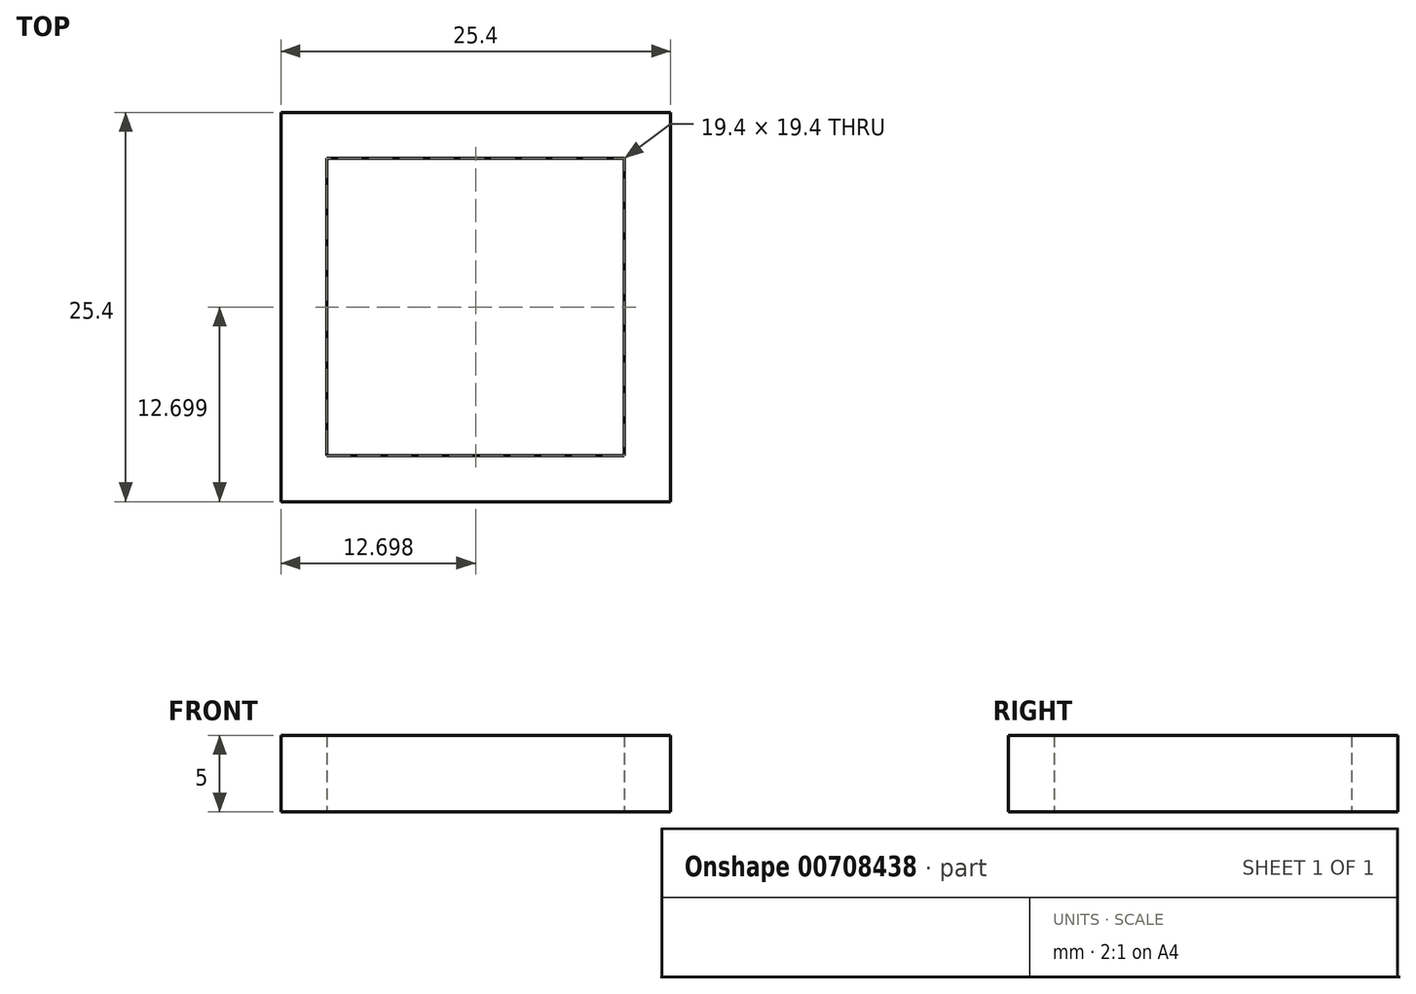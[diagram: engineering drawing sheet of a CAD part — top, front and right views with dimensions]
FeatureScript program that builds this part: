
annotation { "Feature Type Name" : "Feature", "Feature Type Description" : "" }
export const myFeature = defineFeature(function(context is Context, id is Id, definition is map)
    precondition{}
    {
        {
            var Q0;
            Q0=qCreatedBy(makeId("Top.planeOp"),FACE);
            var sketch = newSketch(context, id + "F0", { "sketchPlane" : qUnion([Q0])});
            skLineSegment(sketch, "E0.bottom", {"start": v(-14.47, -13.6) * mm, "end": v(10.93, -13.6) * mm});
            skLineSegment(sketch, "E0.top", {"start": v(-14.47, 11.8) * mm, "end": v(10.93, 11.8) * mm});
            skLineSegment(sketch, "E0.left", {"start": v(-14.47, -13.6) * mm, "end": v(-14.47, 11.8) * mm});
            skLineSegment(sketch, "E0.right", {"start": v(10.93, -13.6) * mm, "end": v(10.93, 11.8) * mm});
            skLineSegment(sketch, "E1.0", {"start": v(-11.47, 8.8) * mm, "end": v(7.93, 8.8) * mm});
            skLineSegment(sketch, "E1.1", {"start": v(-11.47, -10.6) * mm, "end": v(-11.47, 8.8) * mm});
            skLineSegment(sketch, "E1.2", {"start": v(-11.47, -10.6) * mm, "end": v(7.93, -10.6) * mm});
            skLineSegment(sketch, "E1.3", {"start": v(7.93, -10.6) * mm, "end": v(7.93, 8.8) * mm});
            skSolve(sketch);
        }
        {
            var Q0;
            Q0=makeQuery(id+"F0.imprint","IMPRINT",FACE,{"disambiguationData":[TD([[makeQuery(id+"F0.imprint","IMPRINT",EDGE,{"derivedFrom":sQuery(id+"F0.wireOp",EDGE,"E0.bottom")}),1.0]])]});
            extrude(context, id + "F1", {"entities" : qUnion([Q0]), "depth" : 5 * mm, "offsetDistance" : 25 * mm});
        }
    });
